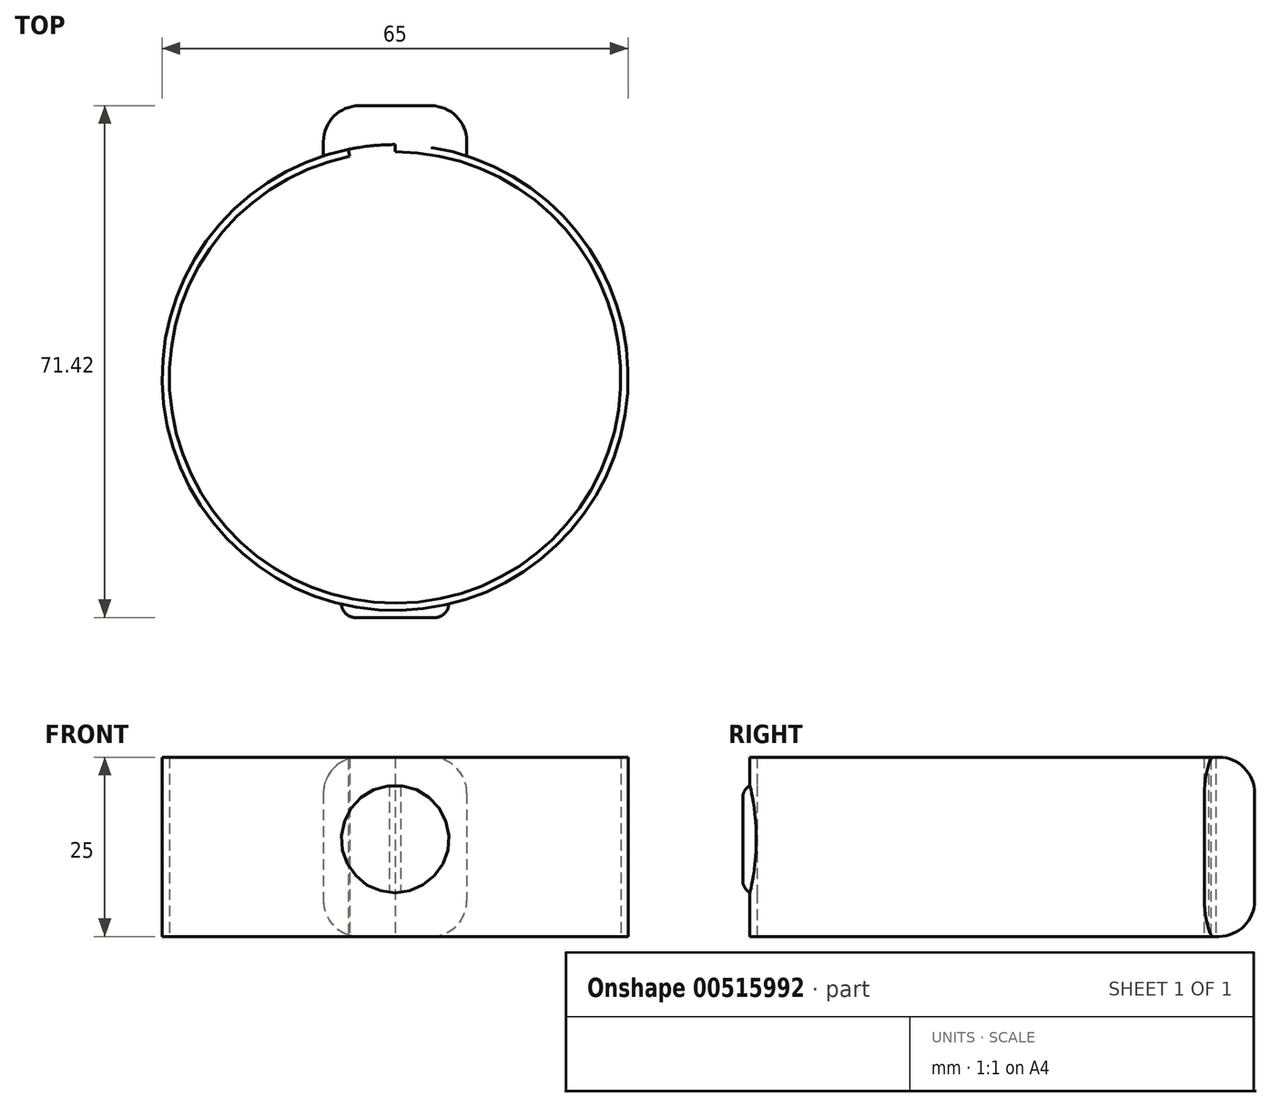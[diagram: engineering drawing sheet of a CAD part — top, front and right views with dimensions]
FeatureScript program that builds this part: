
annotation { "Feature Type Name" : "Feature", "Feature Type Description" : "" }
export const myFeature = defineFeature(function(context is Context, id is Id, definition is map)
    precondition{}
    {
        {
            var Q0;
            Q0=qCreatedBy(makeId("Top.planeOp"),FACE);
            var sketch = newSketch(context, id + "F0", { "sketchPlane" : qUnion([Q0])});
            skArc(sketch, "E0", {"start": v(-6.35, 30.85) * mm, "mid": v(3.2, -31.34) * mm, "end": v(0, 31.5) * mm});
            skCircle(sketch, "E1.0", {"center": v(0, 0) * mm, "radius": 32.5 * mm});
            skLineSegment(sketch, "E2.top", {"start": v(5, 37.92) * mm, "end": v(-5, 37.92) * mm});
            skLineSegment(sketch, "E2.left", {"start": v(10, 30.92) * mm, "end": v(10, 32.92) * mm});
            skLineSegment(sketch, "E2.right", {"start": v(-10, 30.92) * mm, "end": v(-10, 32.92) * mm});
            skPoint(sketch, "E2.middle", {"position": v(0, 34.42) * mm});
            skPoint(sketch, "E3.start.orphan", {"position": v(0, 30.19) * mm});
            skArc(sketch, "E4", {"start": v(10, 30.92) * mm, "mid": v(0, 32.5) * mm, "end": v(-10, 30.92) * mm});
            skPoint(sketch, "E5.visualSharp", {"position": v(-10, 37.92) * mm});
            skArc(sketch, "E5.filletArc", {"start": v(-5, 37.92) * mm, "mid": v(-8.54, 36.46) * mm, "end": v(-10, 32.92) * mm});
            skPoint(sketch, "E6.visualSharp", {"position": v(10, 37.92) * mm});
            skArc(sketch, "E6.filletArc", {"start": v(10, 32.92) * mm, "mid": v(8.54, 36.46) * mm, "end": v(5, 37.92) * mm});
            skLineSegment(sketch, "E7", {"start": v(0, 32.5) * mm, "end": v(0, 31.5) * mm});
            skPoint(sketch, "E8.middle", {"position": v(0, -32.5) * mm});
            skLineSegment(sketch, "E9", {"start": v(-6.35, 30.85) * mm, "end": v(-6.56, 31.83) * mm});
            skPoint(sketch, "E10.orphan", {"position": v(7.69, -33.69) * mm});
            skPoint(sketch, "E11.center.orphan", {"position": v(0, 0.27) * mm});
            skPoint(sketch, "E12.orphan", {"position": v(-7.69, -33.69) * mm});
            skPoint(sketch, "E8.left.end.orphan", {"position": v(7.69, -31.31) * mm});
            skPoint(sketch, "E8.right.end.orphan", {"position": v(-7.69, -31.31) * mm});
            skSolve(sketch);
        }
        {
            var Q0;
            Q0 = qSketchRegion(id + "F0", true);
            extrude(context, id + "F1", {"entities" : qUnion([Q0]), "depth" : 25 * mm, "offsetDistance" : 25 * mm});
        }
        {
            var Q0;
            Q0=qCreatedBy(makeId("Front.planeOp"),FACE);
            cPlane(context, id + "F2", {"entities" : qUnion([Q0]), "cplaneType" : CPlaneType.OFFSET, "offset" : 33.5 * mm, "width" : 150 * mm, "height" : 150 * mm});
        }
        {
            var Q0;
            Q0=makeQuery(id+"F1.opExtrude","CAP_EDGE",EDGE,{"disambiguationData":[OSD([sQuery(id+"F0.wireOp",EDGE,"E6.filletArc")])],"isStart":false});
            var Q1;
            Q1=makeQuery(id+"F1.opExtrude","CAP_EDGE",EDGE,{"disambiguationData":[OSD([sQuery(id+"F0.wireOp",EDGE,"E6.filletArc")])],"isStart":true});
            fillet(context, id + "F3", {"entities" : qUnion([Q0, Q1]), "radius" : 5 * mm, "tangentPropagation" : true, "allowEdgeOverflow" : false});
        }
        {
            var Q0;
            Q0=qCreatedBy(id+"F2.planeOp",FACE);
            var sketch = newSketch(context, id + "F4", { "sketchPlane" : qUnion([Q0])});
            skCircle(sketch, "E13", {"center": v(0, 13.58) * mm, "radius": 7.5 * mm});
            skSolve(sketch);
        }
        {
            var Q0;
            Q0 = qSketchRegion(id + "F4", true);
            extrude(context, id + "F5", {"entities" : qUnion([Q0]), "operationType" : NewBodyOperationType.ADD, "oppositeDirection" : true, "depth" : 2 * mm, "offsetDistance" : 25 * mm});
        }
        {
            var Q0;
            Q0=makeQuery(id+"F5.opExtrude","CAP_EDGE",EDGE,{"disambiguationData":[OSD([sQuery(id+"F4.wireOp",EDGE,"E13")])],"isStart":true});
            fillet(context, id + "F6", {"entities" : qUnion([Q0]), "radius" : 2 * mm, "tangentPropagation" : true, "allowEdgeOverflow" : false});
        }
    });
